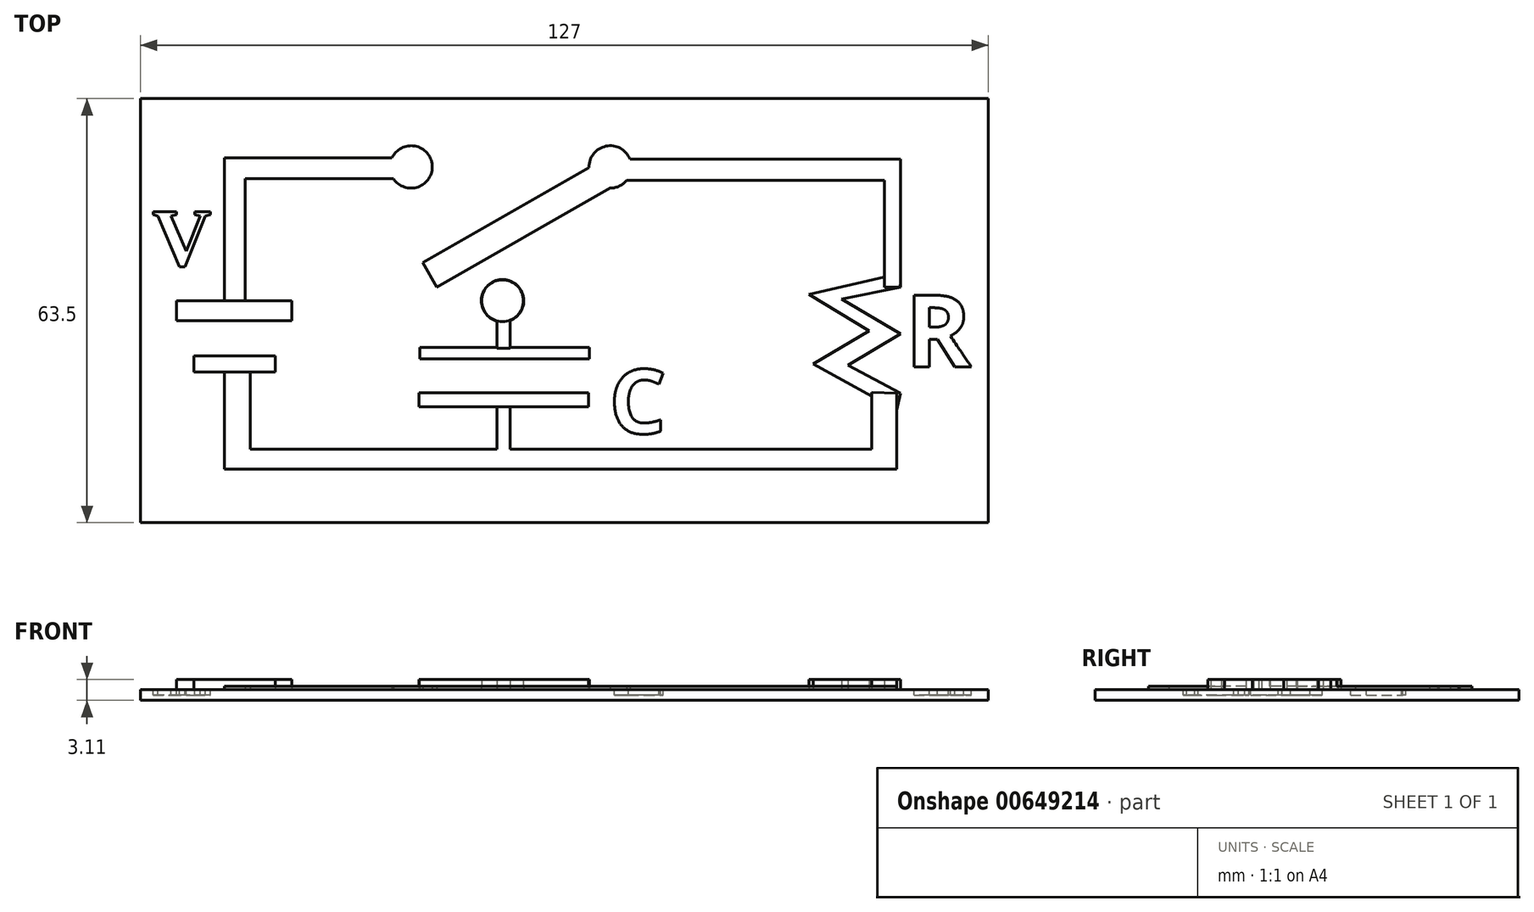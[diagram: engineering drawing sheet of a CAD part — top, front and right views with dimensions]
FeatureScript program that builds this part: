
annotation { "Feature Type Name" : "Feature", "Feature Type Description" : "" }
export const myFeature = defineFeature(function(context is Context, id is Id, definition is map)
    precondition{}
    {
        {
            var Q0;
            Q0=qCreatedBy(makeId("Top.planeOp"),FACE);
            var sketch = newSketch(context, id + "F0", { "sketchPlane" : qUnion([Q0])});
            skLineSegment(sketch, "E0.bottom", {"start": v(0, 0) * mm, "end": v(127, 0) * mm});
            skLineSegment(sketch, "E0.top", {"start": v(0, 63.5) * mm, "end": v(127, 63.5) * mm});
            skLineSegment(sketch, "E0.left", {"start": v(0, 0) * mm, "end": v(0, 63.5) * mm});
            skLineSegment(sketch, "E0.right", {"start": v(127, 0) * mm, "end": v(127, 63.5) * mm});
            skSolve(sketch);
        }
        {
            var Q0;
            Q0=makeQuery(id+"F0.imprint","IMPRINT",FACE,{"disambiguationData":[TD([[makeQuery(id+"F0.imprint","IMPRINT",EDGE,{"derivedFrom":sQuery(id+"F0.wireOp",EDGE,"E0.bottom")}),1.0]])]});
            extrude(context, id + "F1", {"entities" : qUnion([Q0]), "depth" : 1.59 * mm, "offsetDistance" : 25.4 * mm});
        }
        {
            var Q0;
            Q0=makeQuery(id+"F1.opExtrude","CAP_FACE",FACE,{"disambiguationData":[OSD([sQuery(id+"F0.wireOp",EDGE,"E0.bottom"),sQuery(id+"F0.wireOp",EDGE,"E0.top"),sQuery(id+"F0.wireOp",EDGE,"E0.left"),sQuery(id+"F0.wireOp",EDGE,"E0.right")])],"isStart":false});
            var sketch = newSketch(context, id + "F2", { "sketchPlane" : qUnion([Q0])});
            skArc(sketch, "E1", {"start": v(37.9, 51.5) * mm, "mid": v(43.7, 53.5) * mm, "end": v(37.67, 54.64) * mm});
            skArc(sketch, "E2", {"start": v(70.37, 50.1) * mm, "mid": v(71.75, 50.41) * mm, "end": v(72.85, 51.3) * mm});
            skArc(sketch, "E3", {"start": v(55.34, 30.27) * mm, "mid": v(54.08, 36.42) * mm, "end": v(53.42, 30.17) * mm});
            skLineSegment(sketch, "E4", {"start": v(37.67, 54.64) * mm, "end": v(12.54, 54.64) * mm});
            skLineSegment(sketch, "E5", {"start": v(12.54, 54.64) * mm, "end": v(12.54, 33.24) * mm});
            skLineSegment(sketch, "E6", {"start": v(12.54, 22.6) * mm, "end": v(12.54, 8.02) * mm});
            skLineSegment(sketch, "E7", {"start": v(12.54, 8.02) * mm, "end": v(113.29, 8.02) * mm});
            skLineSegment(sketch, "E8", {"start": v(113.29, 8.02) * mm, "end": v(113.29, 19.37) * mm});
            skLineSegment(sketch, "E9", {"start": v(73.31, 54.47) * mm, "end": v(113.85, 54.47) * mm});
            skLineSegment(sketch, "E10", {"start": v(113.85, 54.47) * mm, "end": v(113.85, 36.19) * mm});
            skLineSegment(sketch, "E11", {"start": v(12.54, 33.24) * mm, "end": v(15.68, 33.24) * mm});
            skLineSegment(sketch, "E12", {"start": v(15.68, 33.24) * mm, "end": v(15.68, 51.5) * mm});
            skLineSegment(sketch, "E13", {"start": v(15.68, 51.5) * mm, "end": v(37.9, 51.5) * mm});
            skLineSegment(sketch, "E14", {"start": v(72.85, 51.3) * mm, "end": v(111.43, 51.3) * mm});
            skLineSegment(sketch, "E15", {"start": v(111.43, 51.3) * mm, "end": v(111.43, 35.29) * mm});
            skLineSegment(sketch, "E16", {"start": v(111.43, 35.29) * mm, "end": v(113.63, 35.29) * mm});
            skLineSegment(sketch, "E17", {"start": v(113.63, 35.29) * mm, "end": v(113.82, 35.29) * mm});
            skLineSegment(sketch, "E18", {"start": v(113.82, 35.29) * mm, "end": v(113.85, 36.19) * mm});
            skLineSegment(sketch, "E19", {"start": v(12.54, 22.6) * mm, "end": v(16.45, 22.6) * mm});
            skLineSegment(sketch, "E20", {"start": v(16.45, 22.6) * mm, "end": v(16.45, 11.03) * mm});
            skLineSegment(sketch, "E21", {"start": v(16.45, 11.03) * mm, "end": v(53.42, 11.03) * mm});
            skLineSegment(sketch, "E22", {"start": v(109.53, 11.03) * mm, "end": v(109.53, 19.49) * mm});
            skLineSegment(sketch, "E23", {"start": v(109.53, 19.49) * mm, "end": v(113.29, 19.37) * mm});
            skLineSegment(sketch, "E24", {"start": v(55.34, 30.27) * mm, "end": v(55.34, 26.13) * mm});
            skLineSegment(sketch, "E25", {"start": v(67.2, 53.2) * mm, "end": v(57.57, 47.7) * mm});
            skLineSegment(sketch, "E26", {"start": v(57.57, 47.7) * mm, "end": v(42.27, 38.97) * mm});
            skLineSegment(sketch, "E27", {"start": v(42.27, 38.97) * mm, "end": v(44.39, 35.25) * mm});
            skLineSegment(sketch, "E28", {"start": v(44.39, 35.25) * mm, "end": v(70.37, 50.1) * mm});
            skLineSegment(sketch, "E29.trimOffspring", {"start": v(53.42, 30.17) * mm, "end": v(53.42, 26.13) * mm});
            skPoint(sketch, "E30.orphan", {"position": v(70.37, 51.3) * mm});
            skArc(sketch, "E31.trimOffspring", {"start": v(73.31, 54.47) * mm, "mid": v(69.72, 56.38) * mm, "end": v(67.2, 53.2) * mm});
            skLineSegment(sketch, "E32.trimOffspring", {"start": v(55.34, 11.03) * mm, "end": v(109.53, 11.03) * mm});
            skLineSegment(sketch, "E33", {"start": v(53.42, 26.13) * mm, "end": v(55.34, 26.13) * mm});
            skLineSegment(sketch, "E34", {"start": v(53.42, 17.35) * mm, "end": v(55.34, 17.35) * mm});
            skLineSegment(sketch, "E35.trimOffspring", {"start": v(53.42, 17.35) * mm, "end": v(53.42, 11.03) * mm});
            skLineSegment(sketch, "E36.trimOffspring", {"start": v(55.34, 17.35) * mm, "end": v(55.34, 11.03) * mm});
            skSolve(sketch);
        }
        {
            var Q0;
            Q0=makeQuery(id+"F2.imprint","IMPRINT",FACE,{"disambiguationData":[TD([[makeQuery(id+"F2.imprint","IMPRINT",EDGE,{"derivedFrom":sQuery(id+"F2.wireOp",EDGE,"E1")}),1.0]])]});
            var Q1;
            Q1=makeQuery(id+"F2.imprint","IMPRINT",FACE,{"disambiguationData":[TD([[makeQuery(id+"F2.imprint","IMPRINT",EDGE,{"derivedFrom":sQuery(id+"F2.wireOp",EDGE,"E2")}),1.0]])]});
            var Q2;
            Q2=makeQuery(id+"F2.imprint","IMPRINT",FACE,{"disambiguationData":[TD([[makeQuery(id+"F2.imprint","IMPRINT",EDGE,{"derivedFrom":sQuery(id+"F2.wireOp",EDGE,"E3")}),1.0]])]});
            var Q3;
            Q3=makeQuery(id+"F2.imprint","IMPRINT",FACE,{"disambiguationData":[TD([[makeQuery(id+"F2.imprint","IMPRINT",EDGE,{"derivedFrom":sQuery(id+"F2.wireOp",EDGE,"E6")}),1.0]])]});
            extrude(context, id + "F3", {"entities" : qUnion([Q0, Q1, Q2, Q3]), "operationType" : NewBodyOperationType.ADD, "depth" : 0.5 * mm, "offsetDistance" : 25.4 * mm});
        }
        {
            var Q0;
            Q0=makeQuery(id+"F1.opExtrude","CAP_FACE",FACE,{"disambiguationData":[OSD([sQuery(id+"F0.wireOp",EDGE,"E0.bottom"),sQuery(id+"F0.wireOp",EDGE,"E0.top"),sQuery(id+"F0.wireOp",EDGE,"E0.left"),sQuery(id+"F0.wireOp",EDGE,"E0.right")])],"isStart":false});
            var sketch = newSketch(context, id + "F4", { "sketchPlane" : qUnion([Q0])});
            skLineSegment(sketch, "E37", {"start": v(113.85, 35.29) * mm, "end": v(105.04, 33.49) * mm});
            skLineSegment(sketch, "E38", {"start": v(105.04, 33.49) * mm, "end": v(113.85, 28.27) * mm});
            skLineSegment(sketch, "E39", {"start": v(113.85, 28.27) * mm, "end": v(105.98, 23.56) * mm});
            skLineSegment(sketch, "E40", {"start": v(105.98, 23.56) * mm, "end": v(113.85, 19.37) * mm});
            skLineSegment(sketch, "E41", {"start": v(113.85, 19.37) * mm, "end": v(113.29, 16.86) * mm});
            skLineSegment(sketch, "E42", {"start": v(113.29, 16.86) * mm, "end": v(100.78, 23.76) * mm});
            skLineSegment(sketch, "E43", {"start": v(100.78, 23.76) * mm, "end": v(109.16, 28.7) * mm});
            skLineSegment(sketch, "E44", {"start": v(109.16, 28.7) * mm, "end": v(100.14, 34.17) * mm});
            skLineSegment(sketch, "E45", {"start": v(100.14, 34.17) * mm, "end": v(113.85, 37.37) * mm});
            skLineSegment(sketch, "E46", {"start": v(113.85, 37.37) * mm, "end": v(113.85, 35.29) * mm});
            skSolve(sketch);
        }
        {
            var Q0;
            {var subQ12=sQuery(id+"F4.wireOp",EDGE,"E37");Q0=makeQuery(id+"F4.imprint","IMPRINT",FACE,{"disambiguationData":[TD([[makeQuery(id+"F4.imprint","IMPRINT",EDGE,{"derivedFrom":subQ12}),-1.0]])]});}
            extrude(context, id + "F5", {"entities" : qUnion([Q0]), "operationType" : NewBodyOperationType.ADD, "depth" : 1.52 * mm, "offsetDistance" : 25.4 * mm});
        }
        {
            var Q0;
            Q0=makeQuery(id+"F1.opExtrude","CAP_FACE",FACE,{"disambiguationData":[OSD([sQuery(id+"F0.wireOp",EDGE,"E0.bottom"),sQuery(id+"F0.wireOp",EDGE,"E0.top"),sQuery(id+"F0.wireOp",EDGE,"E0.left"),sQuery(id+"F0.wireOp",EDGE,"E0.right")])],"isStart":false});
            var sketch = newSketch(context, id + "F6", { "sketchPlane" : qUnion([Q0])});
            skLineSegment(sketch, "E47.bottom", {"start": v(5.4, 33.24) * mm, "end": v(22.67, 33.24) * mm});
            skLineSegment(sketch, "E47.top", {"start": v(5.4, 30.27) * mm, "end": v(22.67, 30.27) * mm});
            skLineSegment(sketch, "E47.left", {"start": v(5.4, 33.24) * mm, "end": v(5.4, 30.27) * mm});
            skLineSegment(sketch, "E47.right", {"start": v(22.67, 33.24) * mm, "end": v(22.67, 30.27) * mm});
            skLineSegment(sketch, "E48.bottom", {"start": v(7.99, 24.98) * mm, "end": v(20.22, 24.98) * mm});
            skLineSegment(sketch, "E48.top", {"start": v(7.99, 22.6) * mm, "end": v(20.22, 22.6) * mm});
            skLineSegment(sketch, "E48.left", {"start": v(7.99, 24.98) * mm, "end": v(7.99, 22.6) * mm});
            skLineSegment(sketch, "E48.right", {"start": v(20.22, 24.98) * mm, "end": v(20.22, 22.6) * mm});
            skSolve(sketch);
        }
        {
            var Q0;
            Q0=makeQuery(id+"F6.imprint","IMPRINT",FACE,{"disambiguationData":[TD([[makeQuery(id+"F6.imprint","IMPRINT",EDGE,{"derivedFrom":sQuery(id+"F6.wireOp",EDGE,"E47.top")}),1.0]])]});
            var Q1;
            Q1=makeQuery(id+"F6.imprint","IMPRINT",FACE,{"disambiguationData":[TD([[makeQuery(id+"F6.imprint","IMPRINT",EDGE,{"derivedFrom":sQuery(id+"F6.wireOp",EDGE,"E48.bottom")}),-1.0]])]});
            extrude(context, id + "F7", {"entities" : qUnion([Q0, Q1]), "operationType" : NewBodyOperationType.ADD, "depth" : 1.52 * mm, "offsetDistance" : 25.4 * mm});
        }
        {
            var Q0;
            Q0=makeQuery(id+"F1.opExtrude","CAP_FACE",FACE,{"disambiguationData":[OSD([sQuery(id+"F0.wireOp",EDGE,"E0.bottom"),sQuery(id+"F0.wireOp",EDGE,"E0.top"),sQuery(id+"F0.wireOp",EDGE,"E0.left"),sQuery(id+"F0.wireOp",EDGE,"E0.right")])],"isStart":false});
            var sketch = newSketch(context, id + "F8", { "sketchPlane" : qUnion([Q0])});
            skLineSegment(sketch, "E49.bottom", {"start": v(41.81, 26.23) * mm, "end": v(67.21, 26.23) * mm});
            skLineSegment(sketch, "E49.top", {"start": v(41.81, 24.54) * mm, "end": v(67.21, 24.54) * mm});
            skLineSegment(sketch, "E49.left", {"start": v(41.81, 26.23) * mm, "end": v(41.81, 24.54) * mm});
            skLineSegment(sketch, "E49.right", {"start": v(67.21, 26.23) * mm, "end": v(67.21, 24.54) * mm});
            skLineSegment(sketch, "E50.bottom", {"start": v(41.74, 19.46) * mm, "end": v(67.14, 19.46) * mm});
            skLineSegment(sketch, "E50.top", {"start": v(41.74, 17.35) * mm, "end": v(67.14, 17.35) * mm});
            skLineSegment(sketch, "E50.left", {"start": v(41.74, 19.46) * mm, "end": v(41.74, 17.35) * mm});
            skLineSegment(sketch, "E50.right", {"start": v(67.14, 19.46) * mm, "end": v(67.14, 17.35) * mm});
            skSolve(sketch);
        }
        {
            var Q0;
            Q0=makeQuery(id+"F8.imprint","IMPRINT",FACE,{"disambiguationData":[TD([[makeQuery(id+"F8.imprint","IMPRINT",EDGE,{"derivedFrom":sQuery(id+"F8.wireOp",EDGE,"E49.top")}),1.0]])]});
            var Q1;
            Q1=makeQuery(id+"F8.imprint","IMPRINT",FACE,{"disambiguationData":[TD([[makeQuery(id+"F8.imprint","IMPRINT",EDGE,{"derivedFrom":sQuery(id+"F8.wireOp",EDGE,"E50.bottom")}),-1.0]])]});
            extrude(context, id + "F9", {"entities" : qUnion([Q0, Q1]), "operationType" : NewBodyOperationType.ADD, "depth" : 1.52 * mm, "offsetDistance" : 25.4 * mm});
        }
        {
            var Q0;
            Q0=makeQuery(id+"F1.opExtrude","CAP_FACE",FACE,{"disambiguationData":[OSD([sQuery(id+"F0.wireOp",EDGE,"E0.bottom"),sQuery(id+"F0.wireOp",EDGE,"E0.top"),sQuery(id+"F0.wireOp",EDGE,"E0.left"),sQuery(id+"F0.wireOp",EDGE,"E0.right")])],"isStart":false});
            var sketch = newSketch(context, id + "F10", { "sketchPlane" : qUnion([Q0])});
            skText(sketch, "E51", { "text": "R", "fontName": "OpenSans-Bold.ttf"});
            skText(sketch, "E52", { "text": "V", "fontName": "Tinos-Bold.ttf"});
            skText(sketch, "E53", { "text": "C", "fontName": "OpenSans-Bold.ttf"});
            const initialGuessF10  = {"E51": [0.11454, 0.0233, 1, 0, 0.01085], "E52": [0.00178, 0.0385, 1, 0, 0.00884], "E53": [0.07022, 0.01336, 1, 0, 0.00966]};
            skSetInitialGuess(sketch, initialGuessF10);
            skSolve(sketch);
        }
        {
            var Q0;
            Q0=makeQuery(id+"F10.imprint","IMPRINT",FACE,{"disambiguationData":[TD([[makeQuery(id+"F10.imprint","IMPRINT",EDGE,{"derivedFrom":sQuery(id+"F10.wireOp",EDGE,"E53.sketch_text.stroke-0")}),-1.0]])]});
            var Q1;
            Q1=makeQuery(id+"F10.imprint","IMPRINT",FACE,{"disambiguationData":[TD([[makeQuery(id+"F10.imprint","IMPRINT",EDGE,{"derivedFrom":sQuery(id+"F10.wireOp",EDGE,"E51.sketch_text.stroke-0")}),-1.0]])]});
            var Q2;
            Q2=makeQuery(id+"F10.imprint","IMPRINT",FACE,{"disambiguationData":[TD([[makeQuery(id+"F10.imprint","IMPRINT",EDGE,{"derivedFrom":sQuery(id+"F10.wireOp",EDGE,"E52.sketch_text.stroke-0")}),-1.0]])]});
            extrude(context, id + "F11", {"entities" : qUnion([Q0, Q1, Q2]), "operationType" : NewBodyOperationType.REMOVE, "oppositeDirection" : true, "depth" : 0.8 * mm, "offsetDistance" : 25.4 * mm});
        }
        {
            var Q0;
            Q0=makeQuery(id+"F3.opExtrude","CAP_FACE",FACE,{"disambiguationData":[OSD([sQuery(id+"F2.wireOp",EDGE,"E3"),sQuery(id+"F2.wireOp",EDGE,"E24"),sQuery(id+"F2.wireOp",EDGE,"E29.trimOffspring"),sQuery(id+"F2.wireOp",EDGE,"E33")])],"isStart":false});
            var sketch = newSketch(context, id + "F12", { "sketchPlane" : qUnion([Q0])});
            skCircle(sketch, "E54", {"center": v(54.24, 33.24) * mm, "radius": 3.13 * mm});
            skSolve(sketch);
        }
        {
            var Q0;
            Q0=makeQuery(id+"F12.imprint","IMPRINT",FACE,{"disambiguationData":[TD([[makeQuery(id+"F12.imprint","IMPRINT",EDGE,{"derivedFrom":sQuery(id+"F12.wireOp",EDGE,"E54")}),1.0]])]});
            extrude(context, id + "F13", {"entities" : qUnion([Q0]), "operationType" : NewBodyOperationType.ADD, "depth" : 1.02 * mm, "offsetDistance" : 25.4 * mm});
        }
    });
